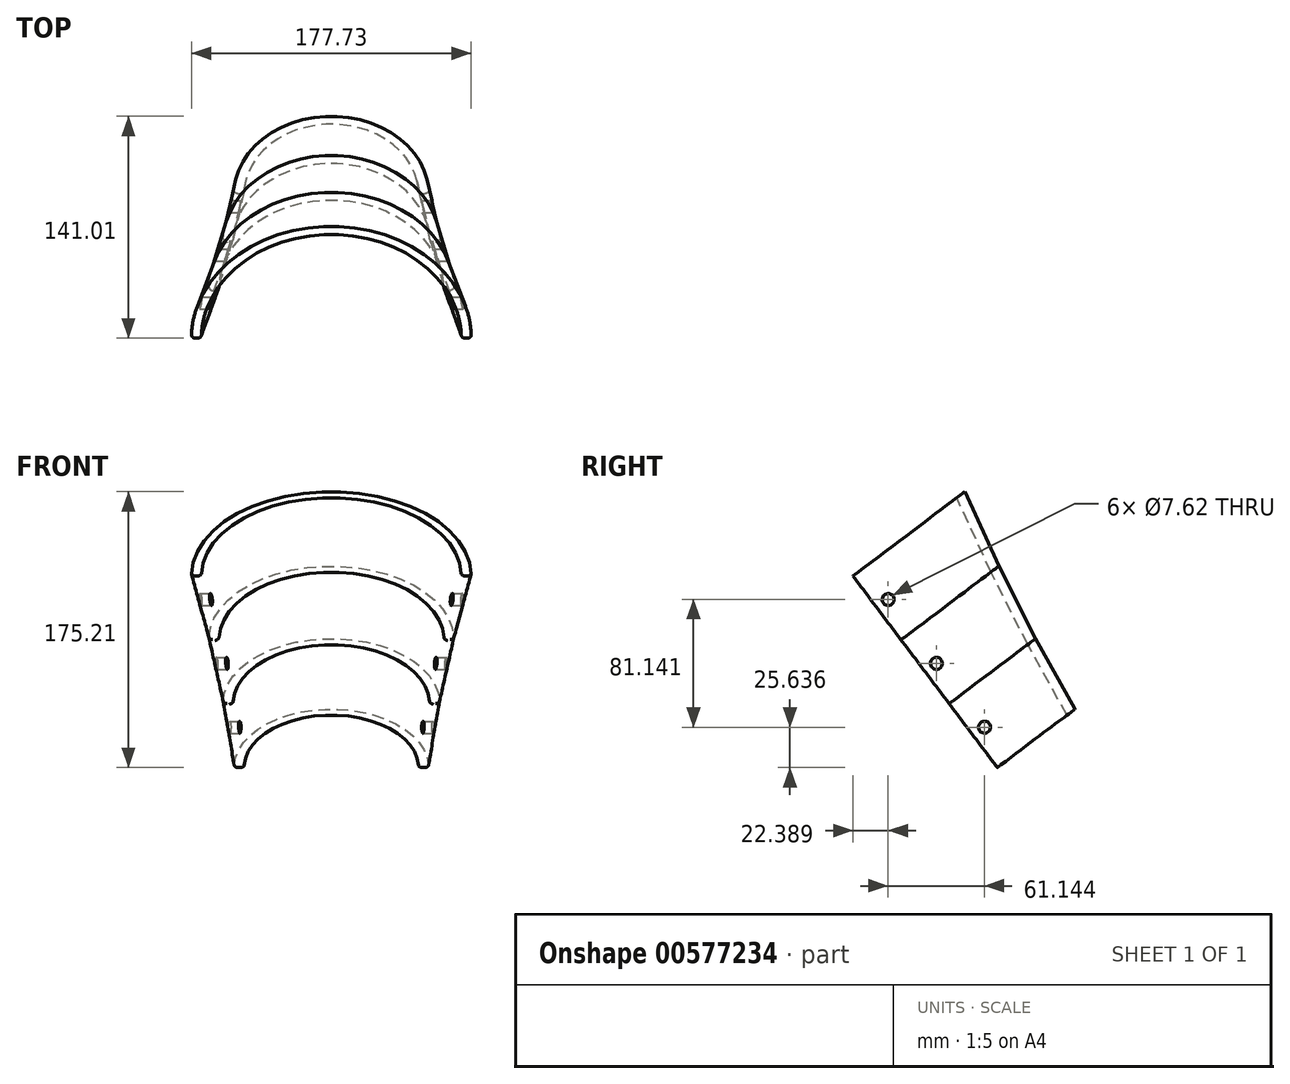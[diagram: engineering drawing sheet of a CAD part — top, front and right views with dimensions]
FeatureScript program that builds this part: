
annotation { "Feature Type Name" : "Feature", "Feature Type Description" : "" }
export const myFeature = defineFeature(function(context is Context, id is Id, definition is map)
    precondition{}
    {
        {
            var Q0;
            Q0=qCreatedBy(makeId("Front.planeOp"),FACE);
            var sketch = newSketch(context, id + "F0", { "sketchPlane" : qUnion([Q0])});
            skLineSegment(sketch, "E0", {"start": v(0, 0) * mm, "end": v(0, 50.8) * mm});
            skLineSegment(sketch, "E1", {"start": v(0, 50.8) * mm, "end": v(68.76, 50.8) * mm, "construction": true});
            skLineSegment(sketch, "E2", {"start": v(0, 0) * mm, "end": v(61.72, 0) * mm});
            skLineSegment(sketch, "E3", {"start": v(61.72, 0) * mm, "end": v(68.76, 50.8) * mm});
            skLineSegment(sketch, "E4", {"start": v(0, 50.8) * mm, "end": v(0, 101.6) * mm});
            skLineSegment(sketch, "E5", {"start": v(0, 101.6) * mm, "end": v(77.84, 101.6) * mm, "construction": true});
            skLineSegment(sketch, "E6", {"start": v(77.84, 101.6) * mm, "end": v(68.76, 50.8) * mm});
            skLineSegment(sketch, "E7", {"start": v(0, 101.6) * mm, "end": v(0, 152.4) * mm});
            skLineSegment(sketch, "E8", {"start": v(0, 152.4) * mm, "end": v(88.9, 152.4) * mm});
            skLineSegment(sketch, "E9", {"start": v(88.9, 152.4) * mm, "end": v(77.84, 101.6) * mm});
            skSolve(sketch);
        }
        {
            var Q0;
            Q0 = qSketchRegion(id + "F0", true);
            var Q1;
            Q1=sQuery(id+"F0.wireOp",EDGE,"E7");
            revolve(context, id + "F1", {"entities" : qUnion([Q0]), "axis" : qUnion([Q1]), "revolveType" : RevolveType.ONE_DIRECTION, "angle" : 180 * degree});
        }
        {
            var Q0;
            Q0=qCreatedBy(makeId("Front.planeOp"),FACE);
            var sketch = newSketch(context, id + "F2", { "sketchPlane" : qUnion([Q0])});
            skLineSegment(sketch, "E10", {"start": v(0, 50.8) * mm, "end": v(62.4, 50.8) * mm, "construction": true});
            skLineSegment(sketch, "E11", {"start": v(0, 50.8) * mm, "end": v(0, 101.6) * mm});
            skLineSegment(sketch, "E12", {"start": v(0, 101.6) * mm, "end": v(71.49, 101.6) * mm, "construction": true});
            skLineSegment(sketch, "E13", {"start": v(71.49, 101.6) * mm, "end": v(62.4, 50.8) * mm});
            skLineSegment(sketch, "E14", {"start": v(0, 101.6) * mm, "end": v(0, 152.4) * mm});
            skLineSegment(sketch, "E15", {"start": v(0, 152.4) * mm, "end": v(82.55, 152.4) * mm});
            skLineSegment(sketch, "E16", {"start": v(82.55, 152.4) * mm, "end": v(71.49, 101.6) * mm});
            skPoint(sketch, "E17.start.orphan", {"position": v(1.44, 0) * mm});
            skLineSegment(sketch, "E18", {"start": v(0, 50.8) * mm, "end": v(0, 0) * mm});
            skLineSegment(sketch, "E19", {"start": v(0, 0) * mm, "end": v(55.37, 0) * mm});
            skLineSegment(sketch, "E20", {"start": v(55.37, 0) * mm, "end": v(62.4, 50.8) * mm});
            skSolve(sketch);
        }
        {
            var Q0;
            Q0 = qSketchRegion(id + "F2", true);
            var Q1;
            Q1=sQuery(id+"F2.wireOp",EDGE,"E14");
            revolve(context, id + "F3", {"operationType" : NewBodyOperationType.REMOVE, "entities" : qUnion([Q0]), "axis" : qUnion([Q1]), "revolveType" : RevolveType.FULL, "oppositeDirection" : true});
        }
        {
            var Q0;
            Q0=makeQuery(id+"F1.opRevolve","CAP_EDGE",EDGE,{"disambiguationData":[OSD([sQuery(id+"F0.wireOp",EDGE,"E9")])],"isStart":true});
            var Q1;
            Q1=makeQuery(id+"F1.opRevolve","CAP_EDGE",EDGE,{"disambiguationData":[OSD([sQuery(id+"F0.wireOp",EDGE,"E6")])],"isStart":true});
            var Q2;
            Q2=makeQuery(id+"F1.opRevolve","CAP_EDGE",EDGE,{"disambiguationData":[OSD([sQuery(id+"F0.wireOp",EDGE,"E3")])],"isStart":true});
            var Q3;
            Q3=makeQuery(id+"F3.boolean.opBoolean","INTERSECT",EDGE,{"disambiguationData":[OD(0.0)],"derivedFrom":[makeQuery(id+"F1.opRevolve","CAP_FACE",FACE,{"disambiguationData":[OSD([sQuery(id+"F0.wireOp",EDGE,"E0"),sQuery(id+"F0.wireOp",EDGE,"E2"),sQuery(id+"F0.wireOp",EDGE,"E3"),sQuery(id+"F0.wireOp",EDGE,"E4"),sQuery(id+"F0.wireOp",EDGE,"E6"),sQuery(id+"F0.wireOp",EDGE,"E7"),sQuery(id+"F0.wireOp",EDGE,"E8"),sQuery(id+"F0.wireOp",EDGE,"E9")])],"isStart":false}),makeQuery(id+"F3.opRevolve","SWEPT_FACE",FACE,{"disambiguationData":[OSD([sQuery(id+"F2.wireOp",EDGE,"E20")])]})]});
            var Q4;
            Q4=makeQuery(id+"F3.boolean.opBoolean","INTERSECT",EDGE,{"disambiguationData":[OD(0.0)],"derivedFrom":[makeQuery(id+"F1.opRevolve","CAP_FACE",FACE,{"disambiguationData":[OSD([sQuery(id+"F0.wireOp",EDGE,"E0"),sQuery(id+"F0.wireOp",EDGE,"E2"),sQuery(id+"F0.wireOp",EDGE,"E3"),sQuery(id+"F0.wireOp",EDGE,"E4"),sQuery(id+"F0.wireOp",EDGE,"E6"),sQuery(id+"F0.wireOp",EDGE,"E7"),sQuery(id+"F0.wireOp",EDGE,"E8"),sQuery(id+"F0.wireOp",EDGE,"E9")])],"isStart":false}),makeQuery(id+"F3.opRevolve","SWEPT_FACE",FACE,{"disambiguationData":[OSD([sQuery(id+"F2.wireOp",EDGE,"E13")])]})]});
            var Q5;
            Q5=makeQuery(id+"F3.boolean.opBoolean","INTERSECT",EDGE,{"disambiguationData":[OD(0.0)],"derivedFrom":[makeQuery(id+"F1.opRevolve","CAP_FACE",FACE,{"disambiguationData":[OSD([sQuery(id+"F0.wireOp",EDGE,"E0"),sQuery(id+"F0.wireOp",EDGE,"E2"),sQuery(id+"F0.wireOp",EDGE,"E3"),sQuery(id+"F0.wireOp",EDGE,"E4"),sQuery(id+"F0.wireOp",EDGE,"E6"),sQuery(id+"F0.wireOp",EDGE,"E7"),sQuery(id+"F0.wireOp",EDGE,"E8"),sQuery(id+"F0.wireOp",EDGE,"E9")])],"isStart":false}),makeQuery(id+"F3.opRevolve","SWEPT_FACE",FACE,{"disambiguationData":[OSD([sQuery(id+"F2.wireOp",EDGE,"E16")])]})]});
            var Q6;
            Q6=makeQuery(id+"F3.boolean.opBoolean","INTERSECT",EDGE,{"disambiguationData":[OD(1.0)],"derivedFrom":[makeQuery(id+"F1.opRevolve","CAP_FACE",FACE,{"disambiguationData":[OSD([sQuery(id+"F0.wireOp",EDGE,"E0"),sQuery(id+"F0.wireOp",EDGE,"E2"),sQuery(id+"F0.wireOp",EDGE,"E3"),sQuery(id+"F0.wireOp",EDGE,"E4"),sQuery(id+"F0.wireOp",EDGE,"E6"),sQuery(id+"F0.wireOp",EDGE,"E7"),sQuery(id+"F0.wireOp",EDGE,"E8"),sQuery(id+"F0.wireOp",EDGE,"E9")])],"isStart":false}),makeQuery(id+"F3.opRevolve","SWEPT_FACE",FACE,{"disambiguationData":[OSD([sQuery(id+"F2.wireOp",EDGE,"E20")])]})]});
            var Q7;
            Q7=makeQuery(id+"F1.opRevolve","CAP_EDGE",EDGE,{"disambiguationData":[OSD([sQuery(id+"F0.wireOp",EDGE,"E3")])],"isStart":false});
            var Q8;
            Q8=makeQuery(id+"F3.boolean.opBoolean","INTERSECT",EDGE,{"disambiguationData":[OD(1.0)],"derivedFrom":[makeQuery(id+"F1.opRevolve","CAP_FACE",FACE,{"disambiguationData":[OSD([sQuery(id+"F0.wireOp",EDGE,"E0"),sQuery(id+"F0.wireOp",EDGE,"E2"),sQuery(id+"F0.wireOp",EDGE,"E3"),sQuery(id+"F0.wireOp",EDGE,"E4"),sQuery(id+"F0.wireOp",EDGE,"E6"),sQuery(id+"F0.wireOp",EDGE,"E7"),sQuery(id+"F0.wireOp",EDGE,"E8"),sQuery(id+"F0.wireOp",EDGE,"E9")])],"isStart":false}),makeQuery(id+"F3.opRevolve","SWEPT_FACE",FACE,{"disambiguationData":[OSD([sQuery(id+"F2.wireOp",EDGE,"E13")])]})]});
            var Q9;
            Q9=makeQuery(id+"F1.opRevolve","CAP_EDGE",EDGE,{"disambiguationData":[OSD([sQuery(id+"F0.wireOp",EDGE,"E6")])],"isStart":false});
            var Q10;
            Q10=makeQuery(id+"F3.boolean.opBoolean","INTERSECT",EDGE,{"disambiguationData":[OD(1.0)],"derivedFrom":[makeQuery(id+"F1.opRevolve","CAP_FACE",FACE,{"disambiguationData":[OSD([sQuery(id+"F0.wireOp",EDGE,"E0"),sQuery(id+"F0.wireOp",EDGE,"E2"),sQuery(id+"F0.wireOp",EDGE,"E3"),sQuery(id+"F0.wireOp",EDGE,"E4"),sQuery(id+"F0.wireOp",EDGE,"E6"),sQuery(id+"F0.wireOp",EDGE,"E7"),sQuery(id+"F0.wireOp",EDGE,"E8"),sQuery(id+"F0.wireOp",EDGE,"E9")])],"isStart":false}),makeQuery(id+"F3.opRevolve","SWEPT_FACE",FACE,{"disambiguationData":[OSD([sQuery(id+"F2.wireOp",EDGE,"E16")])]})]});
            var Q11;
            Q11=makeQuery(id+"F1.opRevolve","CAP_EDGE",EDGE,{"disambiguationData":[OSD([sQuery(id+"F0.wireOp",EDGE,"E9")])],"isStart":false});
            fillet(context, id + "F4", {"entities" : qUnion([Q0, Q1, Q2, Q3, Q4, Q5, Q6, Q7, Q8, Q9, Q10, Q11]), "radius" : 2.54 * mm, "tangentPropagation" : true, "allowEdgeOverflow" : false});
        }
        {
            var Q0;
            Q0=qCreatedBy(makeId("Right.planeOp"),FACE);
            var sketch = newSketch(context, id + "F5", { "sketchPlane" : qUnion([Q0])});
            skLineSegment(sketch, "E21", {"start": v(0, 152.4) * mm, "end": v(88.9, 152.4) * mm, "construction": true});
            skLineSegment(sketch, "E22", {"start": v(0, 0) * mm, "end": v(75.6, 0) * mm, "construction": true});
            skLineSegment(sketch, "E23", {"start": v(0, 0) * mm, "end": v(0, 50.8) * mm, "construction": true});
            skLineSegment(sketch, "E24", {"start": v(0, 50.8) * mm, "end": v(0, 101.6) * mm, "construction": true});
            skLineSegment(sketch, "E25", {"start": v(0, 101.6) * mm, "end": v(0, 152.4) * mm, "construction": true});
            skLineSegment(sketch, "E26", {"start": v(0, 50.8) * mm, "end": v(125.48, 50.8) * mm, "construction": true});
            skLineSegment(sketch, "E27", {"start": v(0, 101.6) * mm, "end": v(125.48, 101.6) * mm, "construction": true});
            skPoint(sketch, "E28", {"position": v(8.89, 25.4) * mm});
            skPoint(sketch, "E28.positionSnap0", {"position": v(0, 25.4) * mm});
            skPoint(sketch, "E29", {"position": v(9.48, 79.82) * mm});
            skPoint(sketch, "E30", {"position": v(0, 76.2) * mm});
            skCircle(sketch, "E31", {"center": v(8.89, 25.4) * mm, "radius": 3.81 * mm});
            skLineSegment(sketch, "E32", {"start": v(0, 76.2) * mm, "end": v(116.66, 76.2) * mm, "construction": true});
            skPoint(sketch, "E33", {"position": v(0, 127) * mm});
            skLineSegment(sketch, "E34", {"start": v(0, 127) * mm, "end": v(163.8, 127) * mm, "construction": true});
            skLineSegment(sketch, "E35", {"start": v(8.89, 25.4) * mm, "end": v(8.89, 161.7) * mm, "construction": true});
            skPoint(sketch, "E36", {"position": v(8.89, 127) * mm});
            skPoint(sketch, "E37", {"position": v(8.89, 76.2) * mm});
            skCircle(sketch, "E38", {"center": v(8.89, 76.2) * mm, "radius": 3.81 * mm});
            skCircle(sketch, "E39", {"center": v(8.89, 127) * mm, "radius": 3.81 * mm});
            skSolve(sketch);
        }
        {
            var Q0;
            Q0 = qSketchRegion(id + "F5", true);
            extrude(context, id + "F6", {"entities" : qUnion([Q0]), "operationType" : NewBodyOperationType.REMOVE, "endBound" : BoundingType.SYMMETRIC, "oppositeDirection" : true, "depth" : 1270 * mm, "offsetDistance" : 25.4 * mm});
        }
        {
            var Q0;
            Q0=makeQuery(id+"F1.opRevolve","SWEPT_BODY",BODY,{"disambiguationData":[OSD([sQuery(id+"F0.wireOp",EDGE,"E0"),sQuery(id+"F0.wireOp",EDGE,"E2"),sQuery(id+"F0.wireOp",EDGE,"E3"),sQuery(id+"F0.wireOp",EDGE,"E4"),sQuery(id+"F0.wireOp",EDGE,"E6"),sQuery(id+"F0.wireOp",EDGE,"E7"),sQuery(id+"F0.wireOp",EDGE,"E8"),sQuery(id+"F0.wireOp",EDGE,"E9")])]});
            var Q1;
            Q1=makeQuery(id+"F1.opRevolve","SWEPT_EDGE",EDGE,{"disambiguationData":[OSD([sQuery(id+"F0.wireOp",EDGE,"E8"),sQuery(id+"F0.wireOp",EDGE,"E9")])]});
            transform(context, id + "F7", {"entities" : qUnion([Q0]), "transformType" : TransformType.TRANSLATION_ENTITY, "oppositeDirectionEntity" : false, "transformLine" : qUnion([Q1]), "makeCopy" : false});
        }
        {
            var Q0;
            Q0=makeQuery(id+"F1.opRevolve","SWEPT_BODY",BODY,{"disambiguationData":[OSD([sQuery(id+"F0.wireOp",EDGE,"E0"),sQuery(id+"F0.wireOp",EDGE,"E2"),sQuery(id+"F0.wireOp",EDGE,"E3"),sQuery(id+"F0.wireOp",EDGE,"E4"),sQuery(id+"F0.wireOp",EDGE,"E6"),sQuery(id+"F0.wireOp",EDGE,"E7"),sQuery(id+"F0.wireOp",EDGE,"E8"),sQuery(id+"F0.wireOp",EDGE,"E9")])]});
            var Q1;
            Q1=sQuery(id+"F0.wireOp",EDGE,"E2");
            transform(context, id + "F8", {"entities" : qUnion([Q0]), "transformType" : TransformType.ROTATION, "transformAxis" : qUnion([Q1]), "angle" : 37 * degree, "makeCopy" : false});
        }
    });
